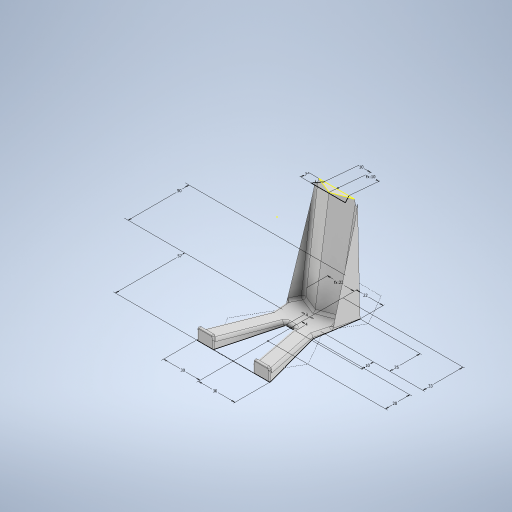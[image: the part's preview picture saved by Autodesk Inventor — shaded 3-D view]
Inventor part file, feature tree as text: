
AUTODESK INVENTOR PART (.ipt)
format: ipt  version: 2023 (Build 270158030, 158C)  size: 533,504 bytes
history: native  units: mm
features: sketch x5, projected_geometry x5, extrude x4, fillet x4
ambient origin geometry x8: Origin, YZ Plane, XZ Plane, XY Plane, X Axis, Y Axis, Z Axis, Center Point
bodies: Body1 (feature_tree)
feature tree (18):
  sketch  "Sketch2"  dims[d4=57.0mm d5=50.0mm]
  extrude  "Extrusion2"  Depth=50.0mm
  extrude  "Extrusion3"  Depth=30.0mm
  extrude  "Extrusion4"  Depth=4.0mm
  extrude  "Extrusion5"  Depth=20.0mm
  fillet  "Fillet1"  Radius=25.0mm
  fillet  "Fillet2"  Radius=33.0mm
  fillet  "Fillet3"  Radius=22.0mm
  fillet  "Fillet4"  Radius=22.0mm
  sketch  "Sketch7"  dims[d16=10.0mm d17=0.0mm d18=0.872665mm d20=2.0mm d21=0.0mm d22=3.0mm d23=3.0mm d24=0.0mm d25=0.0mm d26=6.0mm d27=6.0mm d28=15.0mm d29=80.0mm d30=-0.523599mm d31=13.0mm d32=6.0mm d33=80.0mm d34=-0.349066mm d35=2.0mm d36=2.0mm d37=1.0mm d38=5.0mm d39=10.0mm d40=10.0mm d42=7.0mm]
  sketch  "Sketch4"  dims[d6=30.0mm d7=30.0mm]
  projected_geometry  "Projected Loop1"
  projected_geometry  "Projected Loop2"
  projected_geometry  "Projected Loop3"
  sketch  "Sketch5"  dims[d8=10.0mm d9=4.0mm]
  sketch  "Sketch6"  dims[d10=4.0mm d11=20.0mm d12=25.0mm d13=33.0mm d14=22.0mm d15=22.0mm]
  projected_geometry  "Projected Loop4"
  projected_geometry  "Projected Loop5"
